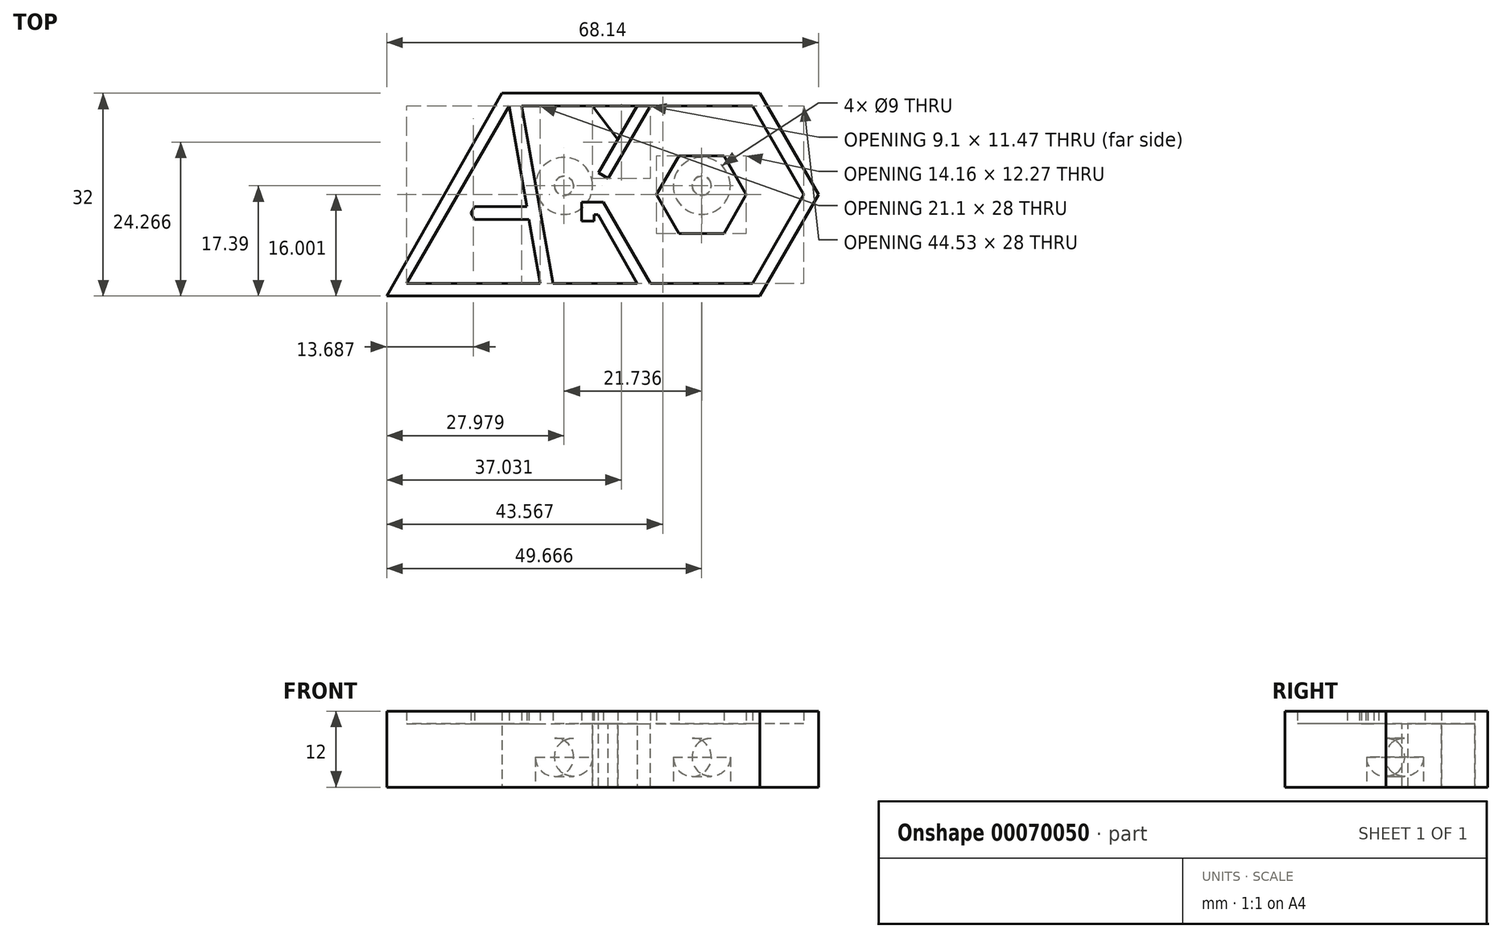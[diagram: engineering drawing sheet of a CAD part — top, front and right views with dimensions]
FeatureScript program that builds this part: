
annotation { "Feature Type Name" : "Feature", "Feature Type Description" : "" }
export const myFeature = defineFeature(function(context is Context, id is Id, definition is map)
    precondition{}
    {
        {
            var Q0;
            Q0=qCreatedBy(makeId("Top.planeOp"),FACE);
            var sketch = newSketch(context, id + "F0", { "sketchPlane" : qUnion([Q0])});
            skLineSegment(sketch, "E0", {"start": v(-33.8, -15.39) * mm, "end": v(-12.7, -15.39) * mm});
            skLineSegment(sketch, "E1", {"start": v(-17.63, 12.61) * mm, "end": v(-33.8, -15.39) * mm});
            skLineSegment(sketch, "E2", {"start": v(-14.47, -5.3) * mm, "end": v(-23.05, -5.3) * mm});
            skPoint(sketch, "E3.endSnap0", {"position": v(-15.16, -1.39) * mm});
            skLineSegment(sketch, "E4", {"start": v(-23.05, -3.3) * mm, "end": v(-14.82, -3.3) * mm});
            skLineSegment(sketch, "E5", {"start": v(-15.63, 12.61) * mm, "end": v(-10.7, -15.39) * mm});
            skLineSegment(sketch, "E6", {"start": v(-23.05, -5.3) * mm, "end": v(-23.62, -4.3) * mm});
            skLineSegment(sketch, "E7", {"start": v(-23.62, -4.3) * mm, "end": v(-23.05, -3.3) * mm});
            skLineSegment(sketch, "E8", {"start": v(20.95, 12.61) * mm, "end": v(12.74, 12.61) * mm, "construction": true});
            skCircle(sketch, "E9.cCircle", {"center": v(12.74, -1.39) * mm, "radius": 14 * mm, "construction": true});
            skLineSegment(sketch, "E9.0", {"start": v(4.65, 12.61) * mm, "end": v(20.82, 12.61) * mm});
            skLineSegment(sketch, "E9.1", {"start": v(20.82, 12.61) * mm, "end": v(28.9, -1.39) * mm});
            skLineSegment(sketch, "E9.2", {"start": v(28.9, -1.39) * mm, "end": v(20.82, -15.39) * mm});
            skLineSegment(sketch, "E9.3", {"start": v(20.82, -15.39) * mm, "end": v(4.65, -15.39) * mm});
            skLineSegment(sketch, "E9.4", {"start": v(4.65, -15.39) * mm, "end": v(-3.43, -1.39) * mm, "construction": true});
            skLineSegment(sketch, "E9.5", {"start": v(-3.43, -1.39) * mm, "end": v(4.65, 12.61) * mm});
            skPoint(sketch, "E9.0.midPoint", {"position": v(12.74, 12.61) * mm});
            skLineSegment(sketch, "E10", {"start": v(-15.63, 12.61) * mm, "end": v(4.65, 12.61) * mm});
            skLineSegment(sketch, "E11", {"start": v(4.65, -15.39) * mm, "end": v(-10.7, -15.39) * mm});
            skLineSegment(sketch, "E12", {"start": v(-2.75, -2.57) * mm, "end": v(-6.2, -2.57) * mm});
            skLineSegment(sketch, "E13", {"start": v(-2.75, -2.57) * mm, "end": v(4.65, -15.39) * mm, "construction": true});
            skLineSegment(sketch, "E14", {"start": v(-2.75, -2.57) * mm, "end": v(4.65, -15.39) * mm});
            skLineSegment(sketch, "E15", {"start": v(-1.97, 1.14) * mm, "end": v(4.65, 12.61) * mm});
            skLineSegment(sketch, "E16", {"start": v(-3.6, -4.57) * mm, "end": v(1.43, -13.39) * mm});
            skCircle(sketch, "E17.cCircle", {"center": v(12.74, -1.39) * mm, "radius": 6.13 * mm, "construction": true});
            skLineSegment(sketch, "E17.0", {"start": v(9.2, 4.74) * mm, "end": v(16.28, 4.74) * mm});
            skLineSegment(sketch, "E17.1", {"start": v(16.28, 4.74) * mm, "end": v(19.82, -1.39) * mm});
            skLineSegment(sketch, "E17.2", {"start": v(19.82, -1.39) * mm, "end": v(16.28, -7.52) * mm});
            skLineSegment(sketch, "E17.3", {"start": v(16.28, -7.52) * mm, "end": v(9.2, -7.52) * mm});
            skLineSegment(sketch, "E17.4", {"start": v(9.2, -7.52) * mm, "end": v(5.65, -1.39) * mm});
            skLineSegment(sketch, "E17.5", {"start": v(5.65, -1.39) * mm, "end": v(9.2, 4.74) * mm});
            skPoint(sketch, "E17.0.midPoint", {"position": v(12.74, 4.74) * mm});
            skLineSegment(sketch, "E18", {"start": v(-19.92, 12.61) * mm, "end": v(-35.8, -15.39) * mm});
            skLineSegment(sketch, "E19.0", {"start": v(-17.63, 14.61) * mm, "end": v(-15.63, 14.61) * mm});
            skLineSegment(sketch, "E19.1", {"start": v(21.97, -17.39) * mm, "end": v(4.65, -17.39) * mm});
            skLineSegment(sketch, "E19.2", {"start": v(31.21, -1.39) * mm, "end": v(21.97, -17.39) * mm});
            skLineSegment(sketch, "E19.3", {"start": v(21.97, 14.61) * mm, "end": v(31.21, -1.39) * mm});
            skLineSegment(sketch, "E19.4", {"start": v(4.65, 14.61) * mm, "end": v(21.97, 14.61) * mm});
            skLineSegment(sketch, "E19.5", {"start": v(4.65, -17.39) * mm, "end": v(-10.7, -17.39) * mm});
            skLineSegment(sketch, "E19.6", {"start": v(-15.63, 14.61) * mm, "end": v(4.65, 14.61) * mm});
            skLineSegment(sketch, "E19.7", {"start": v(-12.7, -17.39) * mm, "end": v(-10.7, -17.39) * mm});
            skLineSegment(sketch, "E19.8", {"start": v(-33.8, -17.39) * mm, "end": v(-12.7, -17.39) * mm});
            skLineSegment(sketch, "E20", {"start": v(-35.8, -15.39) * mm, "end": v(-36.93, -17.39) * mm});
            skLineSegment(sketch, "E21", {"start": v(-36.93, -17.39) * mm, "end": v(-33.8, -17.39) * mm});
            skLineSegment(sketch, "E22", {"start": v(-19.92, 12.61) * mm, "end": v(-18.77, 14.61) * mm});
            skLineSegment(sketch, "E23", {"start": v(-18.77, 14.61) * mm, "end": v(-17.63, 14.61) * mm});
            skLineSegment(sketch, "E24", {"start": v(-3.6, -4.57) * mm, "end": v(2.57, -15.39) * mm});
            skLineSegment(sketch, "E25", {"start": v(-18.77, 14.61) * mm, "end": v(21.97, 14.61) * mm});
            skLineSegment(sketch, "E26", {"start": v(-18.77, 14.61) * mm, "end": v(-36.93, -17.39) * mm});
            skLineSegment(sketch, "E27", {"start": v(-36.93, -17.39) * mm, "end": v(21.97, -17.39) * mm});
            skLineSegment(sketch, "E28", {"start": v(-17.63, 12.61) * mm, "end": v(-14.82, -3.3) * mm});
            skLineSegment(sketch, "E29", {"start": v(-14.47, -5.3) * mm, "end": v(-12.7, -15.39) * mm});
            skLineSegment(sketch, "E30", {"start": v(-1.97, 1.14) * mm, "end": v(-3.53, 2.04) * mm});
            skLineSegment(sketch, "E31", {"start": v(4.65, 12.61) * mm, "end": v(2.57, 12.61) * mm});
            skLineSegment(sketch, "E32", {"start": v(2.57, 12.61) * mm, "end": v(-3.53, 2.04) * mm});
            skLineSegment(sketch, "E33", {"start": v(0.81, 9.57) * mm, "end": v(-4.45, 12.61) * mm});
            skLineSegment(sketch, "E34", {"start": v(-4.24, -4.57) * mm, "end": v(-3.6, -4.57) * mm});
            skLineSegment(sketch, "E35", {"start": v(-6.2, -2.57) * mm, "end": v(-6.2, -5.59) * mm});
            skLineSegment(sketch, "E36", {"start": v(-6.2, -5.59) * mm, "end": v(-4.24, -5.59) * mm});
            skLineSegment(sketch, "E37", {"start": v(-4.24, -4.57) * mm, "end": v(-4.24, -5.59) * mm});
            skLineSegment(sketch, "E38", {"start": v(-0.48, 7.33) * mm, "end": v(-4.45, 12.61) * mm});
            skSolve(sketch);
        }
        {
            var Q0;
            Q0=makeQuery(id+"F0.imprint","IMPRINT",FACE,{"disambiguationData":[TD([[makeQuery(id+"F0.imprint","IMPRINT",EDGE,{"derivedFrom":sQuery(id+"F0.wireOp",EDGE,"E17.0")}),-1.0]])]});
            var Q1;
            {var subQ0=sQuery(id+"F0.wireOp",EDGE,"E15");Q1=makeQuery(id+"F0.imprint","IMPRINT",FACE,{"disambiguationData":[TD([[makeQuery(id+"F0.imprint","IMPRINT",EDGE,{"derivedFrom":subQ0}),1.0]])]});}
            var Q2;
            Q2=makeQuery(id+"F0.imprint","IMPRINT",FACE,{"disambiguationData":[TD([[makeQuery(id+"F0.imprint","IMPRINT",EDGE,{"derivedFrom":sQuery(id+"F0.wireOp",EDGE,"E0")}),-1.0]])]});
            var Q3;
            Q3=makeQuery(id+"F0.imprint","IMPRINT",FACE,{"disambiguationData":[TD([[makeQuery(id+"F0.imprint","IMPRINT",EDGE,{"derivedFrom":sQuery(id+"F0.wireOp",EDGE,"E12")}),1.0]])]});
            var Q4;
            Q4=makeQuery(id+"F0.imprint","IMPRINT",FACE,{"disambiguationData":[TD([[makeQuery(id+"F0.imprint","IMPRINT",EDGE,{"derivedFrom":sQuery(id+"F0.wireOp",EDGE,"E5")}),-1.0]])]});
            var Q5;
            {var subQ0=sQuery(id+"F0.wireOp",EDGE,"E2");Q5=makeQuery(id+"F0.imprint","IMPRINT",FACE,{"disambiguationData":[TD([[makeQuery(id+"F0.imprint","IMPRINT",EDGE,{"derivedFrom":subQ0}),-1.0]])]});}
            var Q6;
            Q6=makeQuery(id+"F0.imprint","IMPRINT",FACE,{"disambiguationData":[TD([[makeQuery(id+"F0.imprint","IMPRINT",EDGE,{"derivedFrom":sQuery(id+"F0.wireOp",EDGE,"E1")}),-1.0]])]});
            extrude(context, id + "F1", {"entities" : qUnion([Q0, Q1, Q2, Q3, Q4, Q5, Q6]), "depth" : 2 * mm});
        }
        {
            var Q0;
            {var subQ3=sQuery(id+"F0.wireOp",EDGE,"E0");Q0=makeQuery(id+"F0.imprint","IMPRINT",FACE,{"disambiguationData":[TD([[makeQuery(id+"F0.imprint","IMPRINT",EDGE,{"derivedFrom":subQ3}),1.0]])]});}
            var Q1;
            {var subQ9=sQuery(id+"F0.wireOp",EDGE,"E5");Q1=makeQuery(id+"F0.imprint","IMPRINT",FACE,{"disambiguationData":[TD([[makeQuery(id+"F0.imprint","IMPRINT",EDGE,{"derivedFrom":subQ9}),1.0]])]});}
            extrude(context, id + "F2", {"entities" : qUnion([Q0, Q1]), "oppositeDirection" : true, "depth" : 10 * mm});
        }
        {
            var Q0;
            Q0=makeQuery(id+"F1.opExtrude","CAP_FACE",FACE,{"disambiguationData":[OSD([sQuery(id+"F0.wireOp",EDGE,"E0"),sQuery(id+"F0.wireOp",EDGE,"E1"),sQuery(id+"F0.wireOp",EDGE,"E2"),sQuery(id+"F0.wireOp",EDGE,"E4"),sQuery(id+"F0.wireOp",EDGE,"E5"),sQuery(id+"F0.wireOp",EDGE,"E6"),sQuery(id+"F0.wireOp",EDGE,"E7"),sQuery(id+"F0.wireOp",EDGE,"E9.0"),sQuery(id+"F0.wireOp",EDGE,"E9.1"),sQuery(id+"F0.wireOp",EDGE,"E9.2"),sQuery(id+"F0.wireOp",EDGE,"E9.3"),sQuery(id+"F0.wireOp",EDGE,"E10"),sQuery(id+"F0.wireOp",EDGE,"E11"),sQuery(id+"F0.wireOp",EDGE,"E12"),sQuery(id+"F0.wireOp",EDGE,"iSGNCPAt-6ZC2-7K8U-PRBr-O0WA7ERkcGIs"),sQuery(id+"F0.wireOp",EDGE,"E14"),sQuery(id+"F0.wireOp",EDGE,"E15"),sQuery(id+"F0.wireOp",EDGE,"r0ZAd0DS-tRZF-mqHU-wFmQ-Bw5r4X2lH74D"),sQuery(id+"F0.wireOp",EDGE,"E19.2"),sQuery(id+"F0.wireOp",EDGE,"E19.3"),sQuery(id+"F0.wireOp",EDGE,"E24"),sQuery(id+"F0.wireOp",EDGE,"qJu2pvME-FPjy-LIMq-Y3gX-S3KwKglR8VOn"),sQuery(id+"F0.wireOp",EDGE,"E25"),sQuery(id+"F0.wireOp",EDGE,"E26"),sQuery(id+"F0.wireOp",EDGE,"E27"),sQuery(id+"F0.wireOp",EDGE,"E28"),sQuery(id+"F0.wireOp",EDGE,"E29")])],"isStart":true});
            var Q1;
            Q1=makeQuery(id+"F1.opExtrude","CAP_FACE",FACE,{"disambiguationData":[OSD([sQuery(id+"F0.wireOp",EDGE,"E17.0"),sQuery(id+"F0.wireOp",EDGE,"E17.1"),sQuery(id+"F0.wireOp",EDGE,"E17.2"),sQuery(id+"F0.wireOp",EDGE,"E17.3"),sQuery(id+"F0.wireOp",EDGE,"E17.4"),sQuery(id+"F0.wireOp",EDGE,"E17.5")])],"isStart":true});
            extrude(context, id + "F3", {"entities" : qUnion([Q0, Q1]), "depth" : 10 * mm});
        }
        {
            var Q0;
            Q0=makeQuery(id+"F2.opExtrude","SWEPT_BODY",BODY,{"disambiguationData":[OSD([sQuery(id+"F0.wireOp",EDGE,"E5"),sQuery(id+"F0.wireOp",EDGE,"E9.0"),sQuery(id+"F0.wireOp",EDGE,"E9.1"),sQuery(id+"F0.wireOp",EDGE,"E9.2"),sQuery(id+"F0.wireOp",EDGE,"E9.3"),sQuery(id+"F0.wireOp",EDGE,"E10"),sQuery(id+"F0.wireOp",EDGE,"E11"),sQuery(id+"F0.wireOp",EDGE,"E12"),sQuery(id+"F0.wireOp",EDGE,"iSGNCPAt-6ZC2-7K8U-PRBr-O0WA7ERkcGIs"),sQuery(id+"F0.wireOp",EDGE,"E14"),sQuery(id+"F0.wireOp",EDGE,"E15"),sQuery(id+"F0.wireOp",EDGE,"r0ZAd0DS-tRZF-mqHU-wFmQ-Bw5r4X2lH74D"),sQuery(id+"F0.wireOp",EDGE,"E17.0"),sQuery(id+"F0.wireOp",EDGE,"E17.1"),sQuery(id+"F0.wireOp",EDGE,"E17.2"),sQuery(id+"F0.wireOp",EDGE,"E17.3"),sQuery(id+"F0.wireOp",EDGE,"E17.4"),sQuery(id+"F0.wireOp",EDGE,"E17.5"),sQuery(id+"F0.wireOp",EDGE,"E24"),sQuery(id+"F0.wireOp",EDGE,"qJu2pvME-FPjy-LIMq-Y3gX-S3KwKglR8VOn")])]});
            var Q1;
            Q1=makeQuery(id+"F2.opExtrude","SWEPT_BODY",BODY,{"disambiguationData":[OSD([sQuery(id+"F0.wireOp",EDGE,"E0"),sQuery(id+"F0.wireOp",EDGE,"E1"),sQuery(id+"F0.wireOp",EDGE,"E2"),sQuery(id+"F0.wireOp",EDGE,"E4"),sQuery(id+"F0.wireOp",EDGE,"E6"),sQuery(id+"F0.wireOp",EDGE,"E7"),sQuery(id+"F0.wireOp",EDGE,"E28"),sQuery(id+"F0.wireOp",EDGE,"E29")])]});
            var Q2;
            Q2=makeQuery(id+"F1.opExtrude","SWEPT_BODY",BODY,{"disambiguationData":[OSD([sQuery(id+"F0.wireOp",EDGE,"E0"),sQuery(id+"F0.wireOp",EDGE,"E1"),sQuery(id+"F0.wireOp",EDGE,"E2"),sQuery(id+"F0.wireOp",EDGE,"E4"),sQuery(id+"F0.wireOp",EDGE,"E5"),sQuery(id+"F0.wireOp",EDGE,"E6"),sQuery(id+"F0.wireOp",EDGE,"E7"),sQuery(id+"F0.wireOp",EDGE,"E9.0"),sQuery(id+"F0.wireOp",EDGE,"E9.1"),sQuery(id+"F0.wireOp",EDGE,"E9.2"),sQuery(id+"F0.wireOp",EDGE,"E9.3"),sQuery(id+"F0.wireOp",EDGE,"E10"),sQuery(id+"F0.wireOp",EDGE,"E11"),sQuery(id+"F0.wireOp",EDGE,"E12"),sQuery(id+"F0.wireOp",EDGE,"iSGNCPAt-6ZC2-7K8U-PRBr-O0WA7ERkcGIs"),sQuery(id+"F0.wireOp",EDGE,"E14"),sQuery(id+"F0.wireOp",EDGE,"E15"),sQuery(id+"F0.wireOp",EDGE,"r0ZAd0DS-tRZF-mqHU-wFmQ-Bw5r4X2lH74D"),sQuery(id+"F0.wireOp",EDGE,"E19.2"),sQuery(id+"F0.wireOp",EDGE,"E19.3"),sQuery(id+"F0.wireOp",EDGE,"E24"),sQuery(id+"F0.wireOp",EDGE,"qJu2pvME-FPjy-LIMq-Y3gX-S3KwKglR8VOn"),sQuery(id+"F0.wireOp",EDGE,"E25"),sQuery(id+"F0.wireOp",EDGE,"E26"),sQuery(id+"F0.wireOp",EDGE,"E27"),sQuery(id+"F0.wireOp",EDGE,"E28"),sQuery(id+"F0.wireOp",EDGE,"E29")])]});
            var Q3;
            Q3=makeQuery(id+"F3.opExtrude","SWEPT_BODY",BODY,{"disambiguationData":[OSD([sQuery(id+"F0.wireOp",EDGE,"E0"),sQuery(id+"F0.wireOp",EDGE,"E1"),sQuery(id+"F0.wireOp",EDGE,"E2"),sQuery(id+"F0.wireOp",EDGE,"E4"),sQuery(id+"F0.wireOp",EDGE,"E5"),sQuery(id+"F0.wireOp",EDGE,"E6"),sQuery(id+"F0.wireOp",EDGE,"E7"),sQuery(id+"F0.wireOp",EDGE,"E9.0"),sQuery(id+"F0.wireOp",EDGE,"E9.1"),sQuery(id+"F0.wireOp",EDGE,"E9.2"),sQuery(id+"F0.wireOp",EDGE,"E9.3"),sQuery(id+"F0.wireOp",EDGE,"E10"),sQuery(id+"F0.wireOp",EDGE,"E11"),sQuery(id+"F0.wireOp",EDGE,"E12"),sQuery(id+"F0.wireOp",EDGE,"iSGNCPAt-6ZC2-7K8U-PRBr-O0WA7ERkcGIs"),sQuery(id+"F0.wireOp",EDGE,"E14"),sQuery(id+"F0.wireOp",EDGE,"E15"),sQuery(id+"F0.wireOp",EDGE,"r0ZAd0DS-tRZF-mqHU-wFmQ-Bw5r4X2lH74D"),sQuery(id+"F0.wireOp",EDGE,"E19.2"),sQuery(id+"F0.wireOp",EDGE,"E19.3"),sQuery(id+"F0.wireOp",EDGE,"E24"),sQuery(id+"F0.wireOp",EDGE,"qJu2pvME-FPjy-LIMq-Y3gX-S3KwKglR8VOn"),sQuery(id+"F0.wireOp",EDGE,"E25"),sQuery(id+"F0.wireOp",EDGE,"E26"),sQuery(id+"F0.wireOp",EDGE,"E27"),sQuery(id+"F0.wireOp",EDGE,"E28"),sQuery(id+"F0.wireOp",EDGE,"E29")])]});
            var Q4;
            Q4=makeQuery(id+"F1.opExtrude","SWEPT_BODY",BODY,{"disambiguationData":[OSD([sQuery(id+"F0.wireOp",EDGE,"E17.0"),sQuery(id+"F0.wireOp",EDGE,"E17.1"),sQuery(id+"F0.wireOp",EDGE,"E17.2"),sQuery(id+"F0.wireOp",EDGE,"E17.3"),sQuery(id+"F0.wireOp",EDGE,"E17.4"),sQuery(id+"F0.wireOp",EDGE,"E17.5")])]});
            var Q5;
            Q5=makeQuery(id+"F3.opExtrude","SWEPT_BODY",BODY,{"disambiguationData":[OSD([sQuery(id+"F0.wireOp",EDGE,"E17.0"),sQuery(id+"F0.wireOp",EDGE,"E17.1"),sQuery(id+"F0.wireOp",EDGE,"E17.2"),sQuery(id+"F0.wireOp",EDGE,"E17.3"),sQuery(id+"F0.wireOp",EDGE,"E17.4"),sQuery(id+"F0.wireOp",EDGE,"E17.5")])]});
            booleanBodies(context, id + "F4", {"operationType" : BooleanOperationType.UNION, "tools" : qUnion([Q0, Q1, Q2, Q3, Q4, Q5])});
        }
        {
            var Q0;
            {var subQ0=sQuery(id+"F0.wireOp",EDGE,"E17.5");var subQ1=sQuery(id+"F0.wireOp",EDGE,"E17.4");var subQ2=sQuery(id+"F0.wireOp",EDGE,"E17.3");var subQ3=sQuery(id+"F0.wireOp",EDGE,"E17.2");var subQ4=sQuery(id+"F0.wireOp",EDGE,"E17.1");var subQ5=sQuery(id+"F0.wireOp",EDGE,"E17.0");var subQ6=sQuery(id+"F0.wireOp",EDGE,"E29");var subQ7=sQuery(id+"F0.wireOp",EDGE,"E28");var subQ8=sQuery(id+"F0.wireOp",EDGE,"qJu2pvME-FPjy-LIMq-Y3gX-S3KwKglR8VOn");var subQ9=sQuery(id+"F0.wireOp",EDGE,"E24");var subQ10=sQuery(id+"F0.wireOp",EDGE,"r0ZAd0DS-tRZF-mqHU-wFmQ-Bw5r4X2lH74D");var subQ11=sQuery(id+"F0.wireOp",EDGE,"E15");var subQ12=sQuery(id+"F0.wireOp",EDGE,"E14");var subQ13=sQuery(id+"F0.wireOp",EDGE,"iSGNCPAt-6ZC2-7K8U-PRBr-O0WA7ERkcGIs");var subQ14=sQuery(id+"F0.wireOp",EDGE,"E12");var subQ15=sQuery(id+"F0.wireOp",EDGE,"E11");var subQ16=sQuery(id+"F0.wireOp",EDGE,"E10");var subQ17=sQuery(id+"F0.wireOp",EDGE,"E9.3");var subQ18=sQuery(id+"F0.wireOp",EDGE,"E9.2");var subQ19=sQuery(id+"F0.wireOp",EDGE,"E9.1");var subQ20=sQuery(id+"F0.wireOp",EDGE,"E9.0");var subQ21=sQuery(id+"F0.wireOp",EDGE,"E7");var subQ22=sQuery(id+"F0.wireOp",EDGE,"E6");var subQ23=sQuery(id+"F0.wireOp",EDGE,"E5");var subQ24=sQuery(id+"F0.wireOp",EDGE,"E4");var subQ25=sQuery(id+"F0.wireOp",EDGE,"E2");var subQ26=sQuery(id+"F0.wireOp",EDGE,"E1");var subQ27=sQuery(id+"F0.wireOp",EDGE,"E0");Q0=makeQuery(id+"F4.opBoolean","MERGE",FACE,{"derivedFrom":[makeQuery(id+"F2.opExtrude","CAP_FACE",FACE,{"disambiguationData":[OSD([subQ27,subQ26,subQ25,subQ24,subQ22,subQ21,subQ7,subQ6])],"isStart":false}),makeQuery(id+"F2.opExtrude","CAP_FACE",FACE,{"disambiguationData":[OSD([subQ23,subQ20,subQ19,subQ18,subQ17,subQ16,subQ15,subQ14,subQ13,subQ12,subQ11,subQ10,subQ5,subQ4,subQ3,subQ2,subQ1,subQ0,subQ9,subQ8])],"isStart":false}),makeQuery(id+"F3.opExtrude","CAP_FACE",FACE,{"disambiguationData":[OSD([subQ27,subQ26,subQ25,subQ24,subQ23,subQ22,subQ21,subQ20,subQ19,subQ18,subQ17,subQ16,subQ15,subQ14,subQ13,subQ12,subQ11,subQ10,sQuery(id+"F0.wireOp",EDGE,"E19.2"),sQuery(id+"F0.wireOp",EDGE,"E19.3"),subQ9,subQ8,sQuery(id+"F0.wireOp",EDGE,"E25"),sQuery(id+"F0.wireOp",EDGE,"E26"),sQuery(id+"F0.wireOp",EDGE,"E27"),subQ7,subQ6])],"isStart":false}),makeQuery(id+"F3.opExtrude","CAP_FACE",FACE,{"disambiguationData":[OSD([subQ5,subQ4,subQ3,subQ2,subQ1,subQ0])],"isStart":false})]});}
            var sketch = newSketch(context, id + "F5", { "sketchPlane" : qUnion([Q0])});
            skCircle(sketch, "E39", {"center": v(12.79, 0) * mm, "radius": 4.5 * mm});
            skCircle(sketch, "E40", {"center": v(-8.95, 0) * mm, "radius": 4.5 * mm});
            skSolve(sketch);
        }
        {
            var Q0;
            Q0=makeQuery(id+"F5.imprint","IMPRINT",FACE,{"disambiguationData":[TD([[makeQuery(id+"F5.imprint","IMPRINT",EDGE,{"derivedFrom":sQuery(id+"F5.wireOp",EDGE,"E39")}),1.0]])]});
            var Q1;
            Q1=makeQuery(id+"F5.imprint","IMPRINT",FACE,{"disambiguationData":[TD([[makeQuery(id+"F5.imprint","IMPRINT",EDGE,{"derivedFrom":sQuery(id+"F5.wireOp",EDGE,"E40")}),1.0]])]});
            extrude(context, id + "F6", {"entities" : qUnion([Q0, Q1]), "operationType" : NewBodyOperationType.REMOVE, "oppositeDirection" : true, "depth" : 7.75 * mm});
        }
        {
            var Q0;
            Q0=makeQuery(id+"F6.boolean.opBoolean","COPY",EDGE,{"derivedFrom":makeQuery(id+"F6.opExtrude","CAP_EDGE",EDGE,{"disambiguationData":[OSD([sQuery(id+"F5.wireOp",EDGE,"E39")])],"isStart":false})});
            var Q1;
            Q1=makeQuery(id+"F6.boolean.opBoolean","COPY",EDGE,{"derivedFrom":makeQuery(id+"F6.opExtrude","CAP_EDGE",EDGE,{"disambiguationData":[OSD([sQuery(id+"F5.wireOp",EDGE,"E40")])],"isStart":false})});
            fillet(context, id + "F7", {"entities" : qUnion([Q0, Q1]), "radius" : 3.02 * mm, "tangentPropagation" : true, "allowEdgeOverflow" : false});
        }
        {
            var Q0;
            {var subQ0=sQuery(id+"F0.wireOp",EDGE,"E33");Q0=makeQuery(id+"F0.imprint","IMPRINT",FACE,{"disambiguationData":[TD([[makeQuery(id+"F0.imprint","IMPRINT",EDGE,{"derivedFrom":subQ0}),1.0]])]});}
            var Q1;
            {var subQ3=sQuery(id+"F0.wireOp",EDGE,"E33");Q1=makeQuery(id+"F0.imprint","IMPRINT",FACE,{"disambiguationData":[TD([[makeQuery(id+"F0.imprint","IMPRINT",EDGE,{"derivedFrom":subQ3}),-1.0]])]});}
            extrude(context, id + "F8", {"entities" : qUnion([Q0, Q1]), "depth" : 2 * mm, "hasSecondDirection" : true, "secondDirectionOppositeDirection" : true, "secondDirectionDepth" : 10 * mm});
        }
        {
            var Q0;
            Q0=makeQuery(id+"F2.opExtrude","SWEPT_BODY",BODY,{"disambiguationData":[OSD([sQuery(id+"F0.wireOp",EDGE,"E5"),sQuery(id+"F0.wireOp",EDGE,"E9.0"),sQuery(id+"F0.wireOp",EDGE,"E9.1"),sQuery(id+"F0.wireOp",EDGE,"E9.2"),sQuery(id+"F0.wireOp",EDGE,"E9.3"),sQuery(id+"F0.wireOp",EDGE,"E10"),sQuery(id+"F0.wireOp",EDGE,"E11"),sQuery(id+"F0.wireOp",EDGE,"E12"),sQuery(id+"F0.wireOp",EDGE,"E14"),sQuery(id+"F0.wireOp",EDGE,"E15"),sQuery(id+"F0.wireOp",EDGE,"E17.0"),sQuery(id+"F0.wireOp",EDGE,"E17.1"),sQuery(id+"F0.wireOp",EDGE,"E17.2"),sQuery(id+"F0.wireOp",EDGE,"E17.3"),sQuery(id+"F0.wireOp",EDGE,"E17.4"),sQuery(id+"F0.wireOp",EDGE,"E17.5"),sQuery(id+"F0.wireOp",EDGE,"E24"),sQuery(id+"F0.wireOp",EDGE,"E30"),sQuery(id+"F0.wireOp",EDGE,"E32"),sQuery(id+"F0.wireOp",EDGE,"E34"),sQuery(id+"F0.wireOp",EDGE,"E35"),sQuery(id+"F0.wireOp",EDGE,"E36"),sQuery(id+"F0.wireOp",EDGE,"E37"),sQuery(id+"F0.wireOp",EDGE,"E38")])]});
            transform(context, id + "F9", {"entities" : qUnion([Q0]), "transformType" : TransformType.TRANSLATION_3D, "dx" : 0 * mm, "dy" : 0 * mm, "dz" : 0 * mm, "makeCopy" : true});
        }
    });
